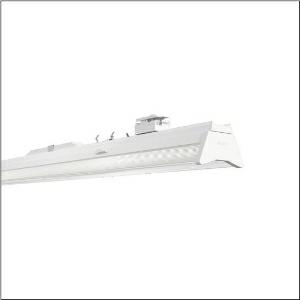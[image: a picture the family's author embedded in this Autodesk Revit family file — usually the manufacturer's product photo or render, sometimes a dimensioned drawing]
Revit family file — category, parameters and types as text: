
# Revit family: licross_r__11_performance_tw_51tm16tnt85x_6a4e
name_source: partatom
category: Lighting Fixtures
units: mm (PartAtom-declared; Revit-internal decimal feet)

## family parameters
Cut with Voids When Loaded = No
Host = Face
Light Source = No
Part Type = Normal
Room Calculation Point = No
Round Connector Dimension = Use Diameter
Shared = No

## types (1)
- --- (1 x LED 2700 K ... 6500 K, 8930 lm, 56 W, 2700K)
    Apparent Load = 56 VA
    CIE Flux Codes = 63 87 95 78 100
    Color Rendering = 80
    Color Temperature = 2700K
    Default Elevation = 1800 mm
    Description = Licross® 11 Performance TW, luminaire insert, of sheet steel, galvanised, coil coated, white, length: 1.500mm, width: 120mm, height: 123mm, LED rated luminous flux: 8.930lm, light colour: 8tw, control gear: DALI DT8, with plug, 5-pole, with phase selection, mains connection: 220..240V, AC, 50/60Hz, rated input power: 56W, internal wiring halogen-free, primary light control with lens, of plastic, primary optical cover: cover, of PMMA, light emission: direct/indirect distribution, primary light characteristic: symmetric, protection rating (complete): IP40, insulation class (complete): insulation class I (protective earthing), certification: CE, ENEC, VDE, UKCA, protection symbol: D if used in an environment without relevant dust loads with corresponding accessories, impact resistance: IK06, permissible ambient temperature for indoor applications: -25..+35°C, corresponds to IFS (International Featured Standards) requirements for safety and quality in the food industry, reducing of maximum allowable ambient temperature of 5°C with ceiling mounting, LABS conformity tested according to VDMA 24364:2018-05, packaging unit: 1 piece
    Height = 114 mm
    Lamp = 1 x LED 2700 K ... 6500 K
    Lamp Light Flux = 8930 lm
    Lamp Power = 56 W
    Lamp count = 1
    Length = 1500 mm
    Luminous efficacy = 159 lm/W
    Manufacturer = Siteco
    ModVariant = No
    Model = 51TM16TNT85X
    Mounting Place = Ceiling
    Mounting Type = Pendant
    Number of Poles = 1
    OnlyDefault = Yes
    Power Factor = 1
    Product Name = Licross® 11 Performance TW
    Product group = luminaire insert | ceiling pendant
    ProductGroupID = 902
    Protection Class = Protection class I
    Protection Degree = IP 40
    RLX_Detail_Level = 1
    RLX_Emergency_Light_Flux = 0 lm
    RLX_Emergency_Type = 0
    RLX_Emergency_Type_DB = No
    RlxData = <blob elided: 30353 chars, md5=cf232584>
    Socket = socket
    Standby Power = 0 W
    System Light Flux = 8930 lm
    System Power = 56 W
    Type Comments = individual setting: CCT=2700K
    Type Image = l_1256138.jpg
    URL = http://relux.com
    VarID = @adj_070087
    Voltage = 0 V
    Weight = 0.00 kg
    Width = 120 mm

## geometry (parser evidence)
native form markers: Blend x4, Sweep x13
no freeform markers — native parametric forms only
